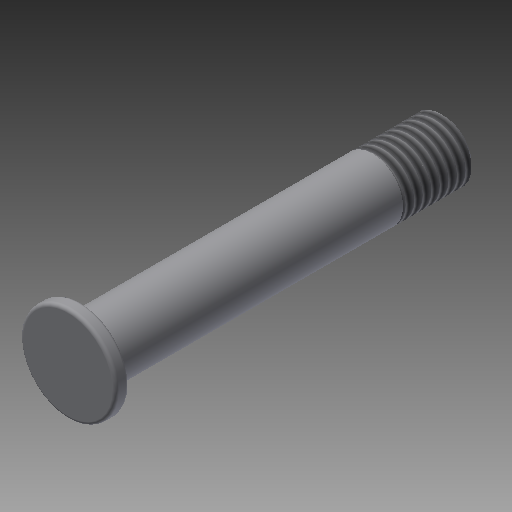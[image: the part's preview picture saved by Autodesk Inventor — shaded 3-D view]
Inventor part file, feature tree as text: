
AUTODESK INVENTOR PART (.ipt)
format: ipt  version: 2019 (Build 230136000, 136)  size: 121,856 bytes
history: native  units: mm
features: extrude x2, chamfer x1, thread x1, fillet x1
ambient origin geometry x8: Origin, YZ Plane, XZ Plane, XY Plane, X Axis, Y Axis, Z Axis, Center Point
bodies: Solido1 (feature_tree)
feature tree (5):
  extrude  "Estrusione1"  Depth=9.0mm
  extrude  "Estrusione2"  Depth=53.0mm TaperAngle=0.0deg
  chamfer  "Smusso1"  Distance=14.0mm
  thread  "Filettatura1"
  fillet  "Raccordo1"  Radius=2.0mm
